# Revit family: Genie_TelescopicBoomLift_(S-85-XC-FE)
name_source: partatom
category: Site
units: mm (PartAtom-declared; Revit-internal decimal feet)

## family parameters
Always vertical = Yes
Cut with Voids When Loaded = No
OmniClass Number = 23.50.85.17
OmniClass Title = Telescoping Platforms
Part Type = Normal
Round Connector Dimension = Use Diameter
Shared = No
Work Plane-Based = No

## types (1)
- S-85 XC FE Telescopic Boom Lift
    Assembly Code = E1030900
    AssetType = Moveable
    BIMObjectName = Genie_TelescopicBoomLift_(S-85-XC-FE)
    ClassificationName = Uniclass2015
    ClassificationValue = TE_30_30_60_10
    Color = Blue
    Cost = 0 $
    Description = S-85 XC FE Telescopic Boom Lift
    DocumentationCertificates = https://www.bimstore.co
    DocumentationInstallationGuide = https://www.bimstore.co
    DocumentationLiterature = https://www.bimstore.co
    DocumentationMaintenance = https://www.bimstore.co
    DocumentationTechnical = https://www.bimstore.co
    DurationUnit = Years
    ExpectedLife = 0
    IfcExportAs = IfcTransportElement
    IfcExportType = IfcTransportElementType
    Keynote = X
    Manufacturer = Genie
    ManufacturerName = Genie
    Model = S-85 XC FE Telescopic Boom Lift
    ModelNumber = S-85 XC FE
    ModelReference = Telescopic Boom Lift
    NBSDescription = Boom lifts
    NBSObjectName = Genie - Boom lifts
    NominalDepth = 0 mm  [stored 0 ft]
    NominalHeight = 0 mm  [stored 0 ft]
    NominalLength = 0 mm  [stored 0 ft]
    ProductionYear = 2025
    SpareParts = https://www.genielift.com
    Type Comments = S-85 XC FE Telescopic Boom Lift
    TypeName = S-85 XC FE Telescopic Boom Lift
    URL = https://www.genielift.com
    WarrantyDurationLabor = 0
    WarrantyDurationParts = 0
    WarrantyDurationUnit = Years
    WarrantyGuarantorLabor = https://www.genielift.com
    WarrantyGuarantorParts = https://www.genielift.com
    _BSBibleVersion = 17
    _BimSpecGuid = 0
    _CurrentRevision = 1
    _DistributedBy = https://www.bimstore.co
    _ObjectUserGuide = https://www.bimstore.co

note: [stored X ft] marks values corroborated as IEEE doubles in the binary element streams (Revit-internal decimal feet)

## geometry (parser evidence)
native form markers: Sweep x45
no freeform markers — native parametric forms only
